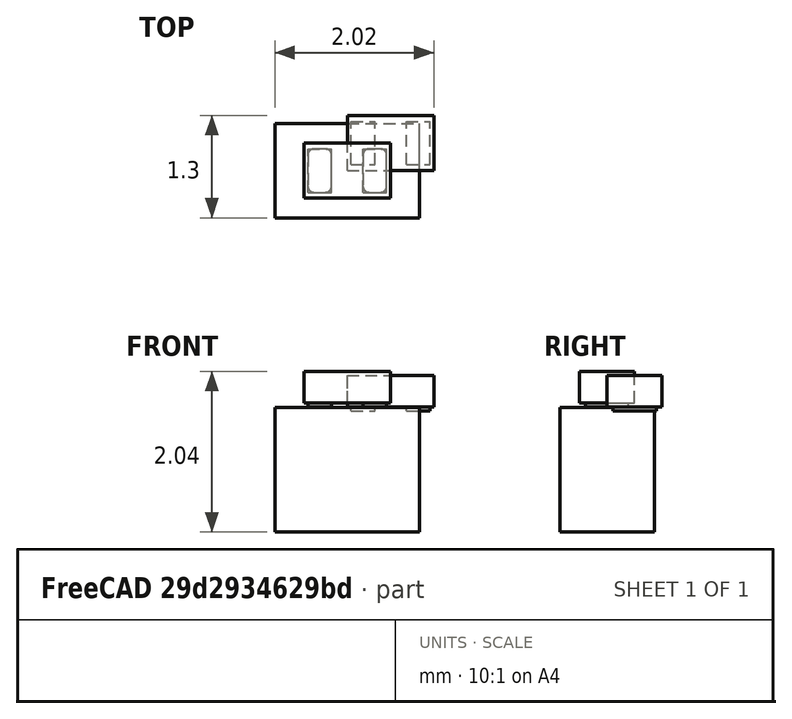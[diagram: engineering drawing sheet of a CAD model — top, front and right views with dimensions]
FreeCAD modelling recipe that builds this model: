
FCSTD DOCUMENT  (FreeCAD 0.17R13522 (Git))
Label: TI_PX1SON
License: All rights reserved
LicenseURL: http://en.wikipedia.org/wiki/All_rights_reserved
objects: Part::Box×3, Part::FeaturePython×3, App::DocumentObjectGroup×1, Part::Feature×1
note: 7 computed .brp shape members not serialized (recipe doc carries the construction recipe); baked Part::Feature solids carry a one-line shape summary decoded from their .brp

FEATURE [Part::Box] Box  label="body"
  AttacherType = Attacher::AttachEngine3D
  Height = 0.4
  Length = 1.1
  Width = 0.7
FEATURE [Part::Box] Box001  label="pin1"
  AttacherType = Attacher::AttachEngine3D
  Height = 0.05
  Length = 0.3
  Placement = pos=(0.05,0.075,-0.05) rot=(0,0,1;0rad)
  Width = 0.55
FEATURE [Part::Box] Box002  label="pin2"
  AttacherType = Attacher::AttachEngine3D
  Height = 0.05
  Length = 0.3
  Placement = pos=(0.75,0.075,-0.05) rot=(0,0,1;0rad)
  Width = 0.55
FEATURE [Part::FeaturePython] FFab_lines  label="FFab"  # a2plus imported part (geometry in sourceFile) (typed FeaturePython)
  fixedPosition = true
FEATURE [Part::FeaturePython] TopPads  # a2plus imported part (geometry in sourceFile) (typed FeaturePython)
  fixedPosition = true
FEATURE [Part::FeaturePython] newPCB  label="Pcb"  # a2plus imported part (geometry in sourceFile) (typed FeaturePython)
  fixedPosition = true
FEATURE [App::DocumentObjectGroup] TI_PX1SON_DPY_fp
  Group = -> [FFab_lines,TopPads,newPCB]
FEATURE [Part::Feature] Shape  label="TI_PX1SON"
  shape: bbox 1.1 x 0.7 x 0.45 mm, 16 faces (baked)
